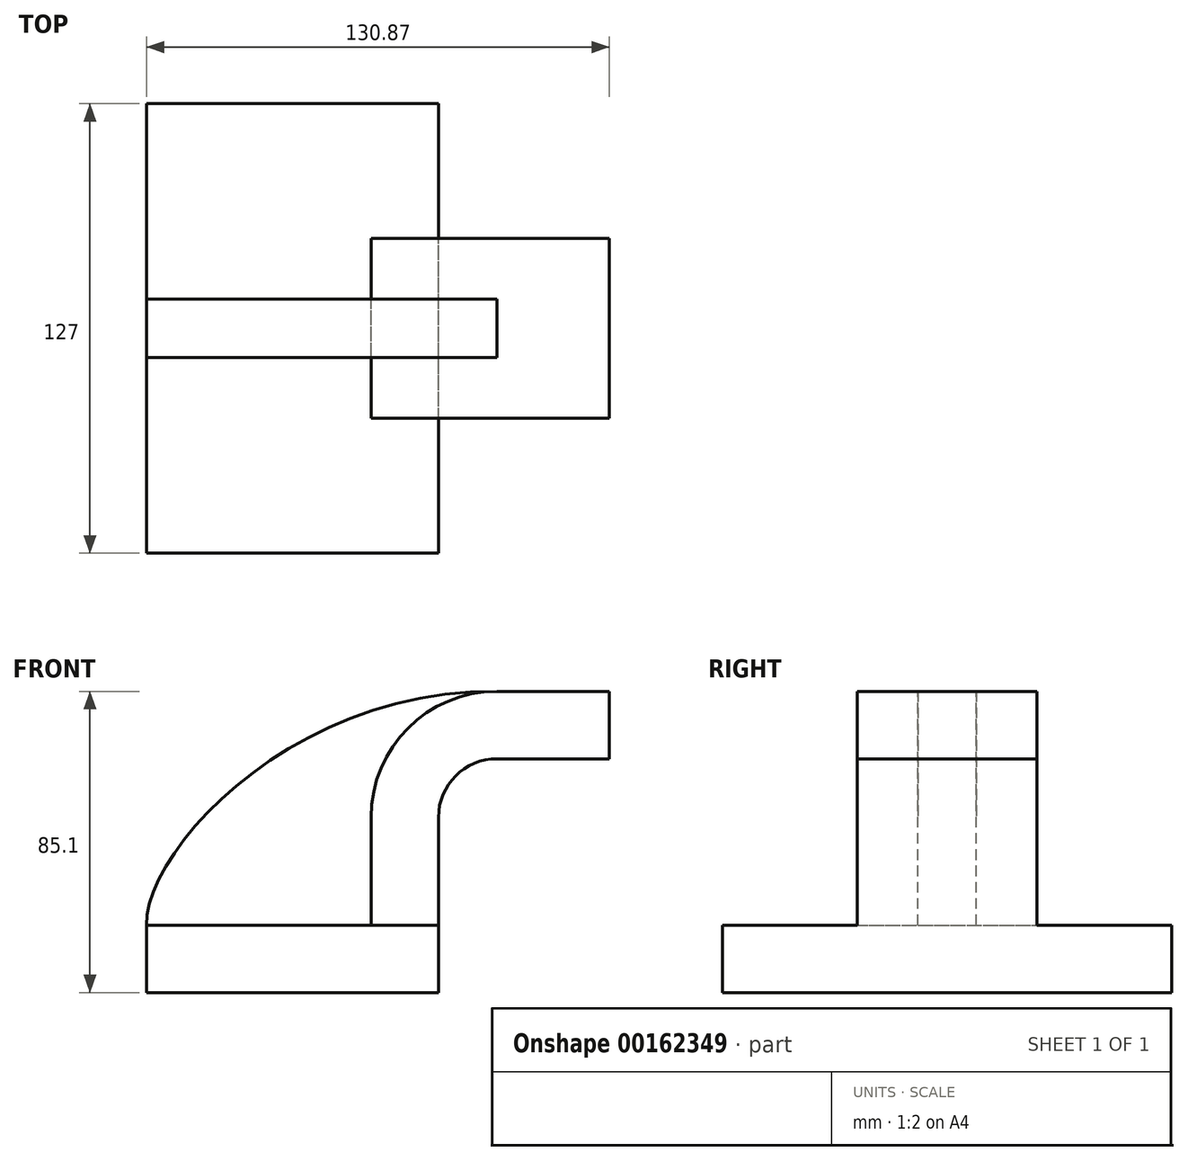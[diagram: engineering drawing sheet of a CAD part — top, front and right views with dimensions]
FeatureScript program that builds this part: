
annotation { "Feature Type Name" : "Feature", "Feature Type Description" : "" }
export const myFeature = defineFeature(function(context is Context, id is Id, definition is map)
    precondition{}
    {
        {
            var Q0;
            Q0=qCreatedBy(makeId("Front.planeOp"),FACE);
            var sketch = newSketch(context, id + "F0", { "sketchPlane" : qUnion([Q0])});
            skLineSegment(sketch, "E0.bottom", {"start": v(-41.28, 9.52) * mm, "end": v(41.28, 9.53) * mm});
            skLineSegment(sketch, "E0.top", {"start": v(-41.28, -9.53) * mm, "end": v(41.28, -9.53) * mm});
            skLineSegment(sketch, "E0.left", {"start": v(-41.28, 9.52) * mm, "end": v(-41.27, -9.53) * mm});
            skLineSegment(sketch, "E0.right", {"start": v(41.28, 9.53) * mm, "end": v(41.28, -9.52) * mm});
            skPoint(sketch, "E0.middle", {"position": v(0, 0) * mm});
            skLineSegment(sketch, "E1.bottom", {"start": v(122.6, 45.08) * mm, "end": v(71.8, 45.08) * mm});
            skLineSegment(sketch, "E1.top", {"start": v(122.6, 76.83) * mm, "end": v(71.8, 76.83) * mm});
            skLineSegment(sketch, "E1.left", {"start": v(122.6, 45.08) * mm, "end": v(122.6, 76.83) * mm});
            skLineSegment(sketch, "E1.right", {"start": v(71.8, 45.08) * mm, "end": v(71.8, 76.84) * mm});
            skPoint(sketch, "E1.middle", {"position": v(97.2, 60.96) * mm});
            skLineSegment(sketch, "E2", {"start": v(41.27, 9.53) * mm, "end": v(41.27, 40) * mm});
            skArc(sketch, "E3", {"start": v(57.78, 56.52) * mm, "mid": v(46.11, 51.68) * mm, "end": v(41.27, 40) * mm});
            skLineSegment(sketch, "E4", {"start": v(57.78, 56.52) * mm, "end": v(89.59, 56.52) * mm});
            skLineSegment(sketch, "E5.0", {"start": v(57.78, 75.57) * mm, "end": v(89.59, 75.57) * mm});
            skArc(sketch, "E5.1", {"start": v(57.78, 75.57) * mm, "mid": v(32.64, 65.15) * mm, "end": v(22.22, 40) * mm});
            skLineSegment(sketch, "E5.2", {"start": v(22.22, 9.53) * mm, "end": v(22.22, 40) * mm});
            skLineSegment(sketch, "E6", {"start": v(89.59, 56.52) * mm, "end": v(89.59, 75.57) * mm});
            skFitSpline(sketch, "E7", {"points": [v(-41.28, 9.52) * mm, v(57.78, 75.57) * mm], "startDerivative": vector(-1.02, 63.64) * mm, "endDerivative": vector(173.35, -1.82) * mm});
            skSolve(sketch);
        }
        {
            var Q0;
            Q0=makeQuery(id+"F0.imprint","IMPRINT",FACE,{"disambiguationData":[TD([[makeQuery(id+"F0.imprint","IMPRINT",EDGE,{"derivedFrom":sQuery(id+"F0.wireOp",EDGE,"E0.top")}),1.0]])]});
            extrude(context, id + "F1", {"entities" : qUnion([Q0]), "endBound" : BoundingType.SYMMETRIC, "depth" : 127 * mm});
        }
        {
            var Q0;
            {var subQ1=sQuery(id+"F0.wireOp",EDGE,"E2");Q0=makeQuery(id+"F0.imprint","IMPRINT",FACE,{"disambiguationData":[TD([[makeQuery(id+"F0.imprint","IMPRINT",EDGE,{"derivedFrom":subQ1}),1.0]])]});}
            var Q1;
            {var subQ5=sQuery(id+"F0.wireOp",EDGE,"E6");Q1=makeQuery(id+"F0.imprint","IMPRINT",FACE,{"disambiguationData":[TD([[makeQuery(id+"F0.imprint","IMPRINT",EDGE,{"derivedFrom":subQ5}),1.0]])]});}
            extrude(context, id + "F2", {"entities" : qUnion([Q0, Q1]), "operationType" : NewBodyOperationType.ADD, "endBound" : BoundingType.SYMMETRIC, "depth" : 50.8 * mm});
        }
        {
            var Q0;
            Q0=makeQuery(id+"F0.imprint","IMPRINT",FACE,{"disambiguationData":[TD([[makeQuery(id+"F0.imprint","IMPRINT",EDGE,{"derivedFrom":sQuery(id+"F0.wireOp",EDGE,"E5.1")}),-1.0]])]});
            extrude(context, id + "F3", {"entities" : qUnion([Q0]), "endBound" : BoundingType.SYMMETRIC, "depth" : 16.5 * mm});
        }
    });
